# Revit family: Slim_Line_Q7_ZUr_FOl
name_source: partatom
category: HLS-Bauteile
units: mm (PartAtom-declared; Revit-internal decimal feet)

## family parameters
Arbeitsebenenbasiert = Nein
Beim Laden mit Abzugskörper schneiden = Nein
Bemaßung runder Anschluss = Durchmesser verwenden
Gemeinsam genutzt = Nein
Immer vertikal = Ja
Klassifizierung = Keine
Raumberechnungspunkt = Nein
Teiletyp = Normal

## types (1)
- Slim_Line_Q7_ZUr_FOl
    B = 650 mm  [stored 2.13255 ft]
    Beschreibung = Gerät
    Classification.OmniClass.23.Description = Pre Fabricated Air Handling Units
    Classification.OmniClass.23.Number = 23-33 25 19
    H = 2050 mm  [stored 6.72572 ft]
    Hersteller = Hansa
    L = 650 mm  [stored 2.13255 ft]
    Modell = Slim-Line-Q7
    RLT_Material_außen = Stahlblech verzinkt + RAL 9002
    RLT_Volumenstrom_max = 1505 m³/h
    Vorgabe-Ansicht = 0 mm  [stored 0 ft]

note: [stored X ft] marks values corroborated as IEEE doubles in the binary element streams (Revit-internal decimal feet)

## geometry (parser evidence)
native form markers: Sweep x3
no freeform markers — native parametric forms only
